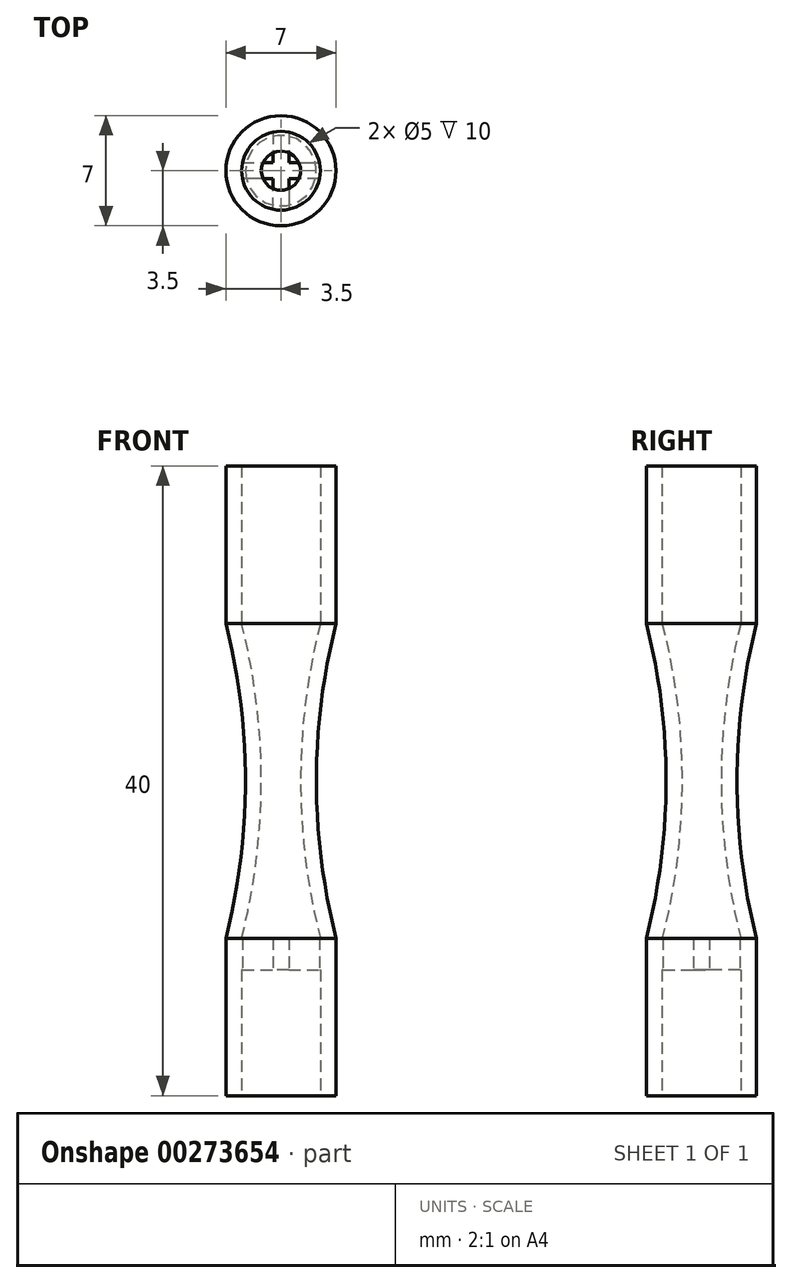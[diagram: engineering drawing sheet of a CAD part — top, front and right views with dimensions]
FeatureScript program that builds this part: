
annotation { "Feature Type Name" : "Feature", "Feature Type Description" : "" }
export const myFeature = defineFeature(function(context is Context, id is Id, definition is map)
    precondition{}
    {
        {
            var Q0;
            Q0=qCreatedBy(makeId("Front.planeOp"),FACE);
            var sketch = newSketch(context, id + "F0", { "sketchPlane" : qUnion([Q0])});
            skLineSegment(sketch, "E0", {"start": v(0, 0) * mm, "end": v(0, 40) * mm});
            skLineSegment(sketch, "E1", {"start": v(0, 0) * mm, "end": v(2.5, 0) * mm});
            skLineSegment(sketch, "E2", {"start": v(2.5, 0) * mm, "end": v(2.5, 10) * mm});
            skLineSegment(sketch, "E3", {"start": v(0, 40) * mm, "end": v(2.5, 40) * mm});
            skLineSegment(sketch, "E4", {"start": v(2.5, 40) * mm, "end": v(2.5, 30) * mm});
            skArc(sketch, "E5", {"start": v(2.5, 30) * mm, "mid": v(1.25, 20) * mm, "end": v(2.5, 10) * mm});
            skLineSegment(sketch, "E6", {"start": v(1.25, 20) * mm, "end": v(0, 20) * mm});
            skLineSegment(sketch, "E7", {"start": v(2.5, 0) * mm, "end": v(3.5, 0) * mm});
            skLineSegment(sketch, "E8", {"start": v(3.5, 0) * mm, "end": v(3.5, 10) * mm});
            skLineSegment(sketch, "E9", {"start": v(2.5, 40) * mm, "end": v(3.5, 40) * mm});
            skLineSegment(sketch, "E10", {"start": v(3.5, 40) * mm, "end": v(3.5, 30) * mm});
            skArc(sketch, "E11", {"start": v(3.5, 30) * mm, "mid": v(2.25, 20) * mm, "end": v(3.5, 10) * mm});
            skLineSegment(sketch, "E12", {"start": v(1.25, 20) * mm, "end": v(2.25, 20) * mm});
            skSolve(sketch);
        }
        {
            var Q0;
            Q0=qCreatedBy(makeId("Top.planeOp"),FACE);
            cPlane(context, id + "F1", {"entities" : qUnion([Q0]), "cplaneType" : CPlaneType.OFFSET, "offset" : 10 * mm, "width" : 150 * mm, "height" : 150 * mm});
        }
        {
            var Q0;
            Q0=qCreatedBy(id+"F1.planeOp",FACE);
            var sketch = newSketch(context, id + "F2", { "sketchPlane" : qUnion([Q0])});
            skLineSegment(sketch, "E13", {"start": v(0, 0) * mm, "end": v(0, 2.5) * mm});
            skLineSegment(sketch, "E14", {"start": v(0, 2.5) * mm, "end": v(0.5, 2.5) * mm});
            skLineSegment(sketch, "E15", {"start": v(0.5, 2.5) * mm, "end": v(0.5, 0) * mm});
            skLineSegment(sketch, "E16", {"start": v(0, 2.5) * mm, "end": v(-0.5, 2.5) * mm});
            skLineSegment(sketch, "E17", {"start": v(-0.5, 2.5) * mm, "end": v(-0.5, 0) * mm});
            skLineSegment(sketch, "E18", {"start": v(0, 0) * mm, "end": v(0, 0.5) * mm});
            skLineSegment(sketch, "E19", {"start": v(0, 0.5) * mm, "end": v(2.5, 0.5) * mm});
            skLineSegment(sketch, "E20", {"start": v(2.5, 0.5) * mm, "end": v(2.5, -0.5) * mm});
            skLineSegment(sketch, "E21", {"start": v(2.5, -0.5) * mm, "end": v(-2.5, -0.5) * mm});
            skLineSegment(sketch, "E22", {"start": v(-2.5, -0.5) * mm, "end": v(-2.5, 0.5) * mm});
            skLineSegment(sketch, "E23", {"start": v(-2.5, 0.5) * mm, "end": v(0, 0.5) * mm});
            skLineSegment(sketch, "E24", {"start": v(0.5, 0) * mm, "end": v(0.5, -2.5) * mm});
            skLineSegment(sketch, "E25", {"start": v(0.5, -2.5) * mm, "end": v(-0.5, -2.5) * mm});
            skLineSegment(sketch, "E26", {"start": v(-0.5, -2.5) * mm, "end": v(-0.5, 0) * mm});
            skSolve(sketch);
        }
        {
            var Q0;
            Q0 = qSketchRegion(id + "F2", true);
            extrude(context, id + "F3", {"entities" : qUnion([Q0]), "oppositeDirection" : true, "depth" : 2 * mm});
        }
        {
            var Q0;
            {var subQ1=sQuery(id+"F0.wireOp",EDGE,"E4");Q0=makeQuery(id+"F0.imprint","IMPRINT",FACE,{"disambiguationData":[TD([[makeQuery(id+"F0.imprint","IMPRINT",EDGE,{"derivedFrom":subQ1}),1.0]])]});}
            var Q1;
            {var subQ1=sQuery(id+"F0.wireOp",EDGE,"E2");Q1=makeQuery(id+"F0.imprint","IMPRINT",FACE,{"disambiguationData":[TD([[makeQuery(id+"F0.imprint","IMPRINT",EDGE,{"derivedFrom":subQ1}),-1.0]])]});}
            var Q2;
            Q2=sQuery(id+"F0.wireOp",EDGE,"E0");
            revolve(context, id + "F4", {"operationType" : NewBodyOperationType.ADD, "entities" : qUnion([Q0, Q1]), "axis" : qUnion([Q2]), "revolveType" : RevolveType.FULL});
        }
    });
